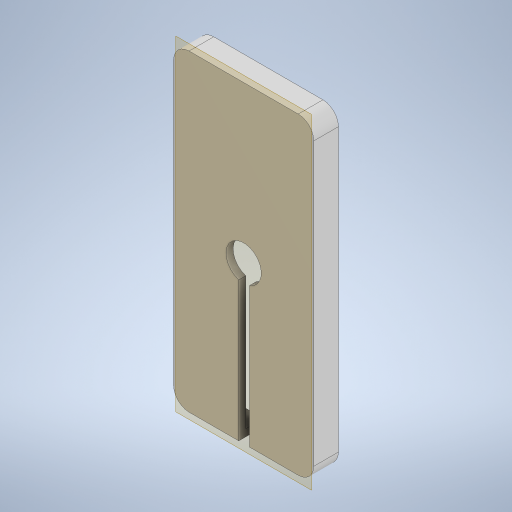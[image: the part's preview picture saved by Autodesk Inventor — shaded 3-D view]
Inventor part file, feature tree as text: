
AUTODESK INVENTOR PART (.ipt)
format: ipt  version: 2023 (Build 270158000, 158)  size: 635,392 bytes
history: native  units: mm
features: other x4, extrude x4, sketch x4, projected_geometry x3
ambient origin geometry x8: Origin, YZ Plane, XZ Plane, XY Plane, X Axis, Y Axis, Z Axis, Center Point
bodies: Solide1 (feature_tree)
feature tree (15):
  other  "Plan de construction1"
  extrude  "Extrusion1"  Depth=0.4mm
  extrude  "Extrusion2"  Depth=2.0mm
  extrude  "Extrusion3"  Depth=2.0mm TaperAngle=0.0deg
  extrude  "Extrusion4"  Depth=2.0mm
  sketch  "Esquisse1"
  other  "Référence1"
  sketch  "Esquisse2"
  projected_geometry  "Boucle projetée1"
  sketch  "Esquisse3"
  projected_geometry  "Boucle projetée2"
  sketch  "Esquisse4"
  projected_geometry  "Boucle projetée3"
  other  "Ensemble1"
  other  "BatterieHolder:1"
